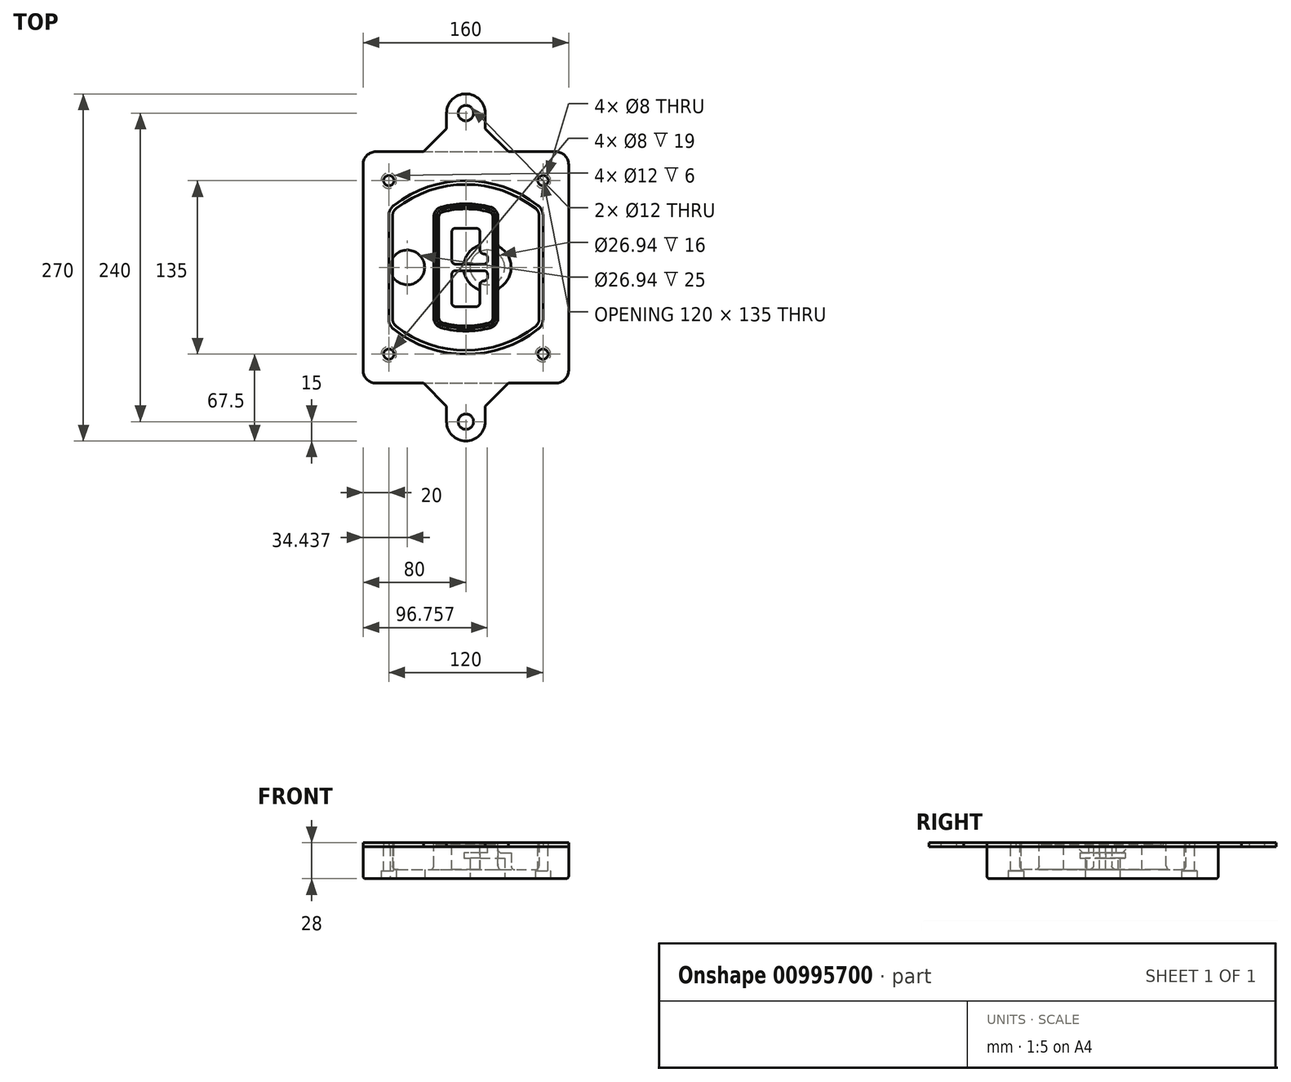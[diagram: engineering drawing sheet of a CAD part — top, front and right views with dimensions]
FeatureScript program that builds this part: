
annotation { "Feature Type Name" : "Feature", "Feature Type Description" : "" }
export const myFeature = defineFeature(function(context is Context, id is Id, definition is map)
    precondition{}
    {
        {
            var Q0;
            Q0=qCreatedBy(makeId("Top.planeOp"),FACE);
            var sketch = newSketch(context, id + "F0", { "sketchPlane" : qUnion([Q0])});
            skPoint(sketch, "E0.rect.middle", {"position": v(0, 0) * mm});
            skLineSegment(sketch, "E1.bottom", {"start": v(-70, -90) * mm, "end": v(70, -90) * mm});
            skLineSegment(sketch, "E1.top", {"start": v(-70, 90) * mm, "end": v(70, 90) * mm});
            skLineSegment(sketch, "E1.left", {"start": v(-80, -80) * mm, "end": v(-80, 80) * mm});
            skLineSegment(sketch, "E1.right", {"start": v(80, -80) * mm, "end": v(80, 80) * mm});
            skLineSegment(sketch, "E2", {"start": v(-80, 90) * mm, "end": v(80, -90) * mm, "construction": true});
            skLineSegment(sketch, "E3", {"start": v(80, 90) * mm, "end": v(-80, -90) * mm, "construction": true});
            skCircle(sketch, "E4", {"center": v(-60, 67.5) * mm, "radius": 4 * mm});
            skCircle(sketch, "E5", {"center": v(60, 67.5) * mm, "radius": 4 * mm});
            skCircle(sketch, "E6", {"center": v(60, -67.5) * mm, "radius": 4 * mm});
            skCircle(sketch, "E7", {"center": v(-60, -67.5) * mm, "radius": 4 * mm});
            skLineSegment(sketch, "E8", {"start": v(-60, 67.5) * mm, "end": v(60, 67.5) * mm, "construction": true});
            skLineSegment(sketch, "E9", {"start": v(60, 67.5) * mm, "end": v(60, -67.5) * mm, "construction": true});
            skLineSegment(sketch, "E10", {"start": v(60, -67.5) * mm, "end": v(-60, -67.5) * mm, "construction": true});
            skLineSegment(sketch, "E11", {"start": v(-60, -67.5) * mm, "end": v(-60, 67.5) * mm, "construction": true});
            skLineSegment(sketch, "E12", {"start": v(-60, 40.3) * mm, "end": v(-60, -40.3) * mm});
            skLineSegment(sketch, "E13", {"start": v(60, 40.3) * mm, "end": v(60, -40.3) * mm});
            skArc(sketch, "E14", {"start": v(56.15, 48.18) * mm, "mid": v(0, 67.5) * mm, "end": v(-56.15, 48.18) * mm});
            skArc(sketch, "E15", {"start": v(-56.15, -48.18) * mm, "mid": v(0, -67.5) * mm, "end": v(56.15, -48.18) * mm});
            skLineSegment(sketch, "E16", {"start": v(-60, 0) * mm, "end": v(60, 0) * mm, "construction": true});
            skPoint(sketch, "E17.visualSharp", {"position": v(-60, -45) * mm});
            skArc(sketch, "E17.filletArc", {"start": v(-60, -40.3) * mm, "mid": v(-58.99, -44.68) * mm, "end": v(-56.15, -48.18) * mm});
            skPoint(sketch, "E18.visualSharp", {"position": v(-60, 45) * mm});
            skArc(sketch, "E18.filletArc", {"start": v(-56.15, 48.18) * mm, "mid": v(-58.99, 44.68) * mm, "end": v(-60, 40.3) * mm});
            skPoint(sketch, "E19.visualSharp", {"position": v(60, 45) * mm});
            skArc(sketch, "E19.filletArc", {"start": v(60, 40.3) * mm, "mid": v(58.99, 44.68) * mm, "end": v(56.15, 48.18) * mm});
            skPoint(sketch, "E20.visualSharp", {"position": v(60, -45) * mm});
            skArc(sketch, "E20.filletArc", {"start": v(56.15, -48.18) * mm, "mid": v(58.99, -44.68) * mm, "end": v(60, -40.3) * mm});
            skPoint(sketch, "E21.visualSharp", {"position": v(-80, 90) * mm});
            skArc(sketch, "E21.filletArc", {"start": v(-70, 90) * mm, "mid": v(-77.07, 87.07) * mm, "end": v(-80, 80) * mm});
            skPoint(sketch, "E22.visualSharp", {"position": v(80, 90) * mm});
            skArc(sketch, "E22.filletArc", {"start": v(80, 80) * mm, "mid": v(77.07, 87.07) * mm, "end": v(70, 90) * mm});
            skPoint(sketch, "E23.visualSharp", {"position": v(80, -90) * mm});
            skArc(sketch, "E23.filletArc", {"start": v(70, -90) * mm, "mid": v(77.07, -87.07) * mm, "end": v(80, -80) * mm});
            skPoint(sketch, "E24.visualSharp", {"position": v(-80, -90) * mm});
            skArc(sketch, "E24.filletArc", {"start": v(-80, -80) * mm, "mid": v(-77.07, -87.07) * mm, "end": v(-70, -90) * mm});
            skArc(sketch, "E25.0", {"start": v(57, 40.3) * mm, "mid": v(56.3, 43.36) * mm, "end": v(54.3, 45.81) * mm});
            skLineSegment(sketch, "E25.1", {"start": v(57, 40.3) * mm, "end": v(57, -40.3) * mm});
            skArc(sketch, "E25.2", {"start": v(54.3, -45.81) * mm, "mid": v(56.3, -43.36) * mm, "end": v(57, -40.3) * mm});
            skArc(sketch, "E25.3", {"start": v(-54.3, -45.81) * mm, "mid": v(0, -64.5) * mm, "end": v(54.3, -45.81) * mm});
            skArc(sketch, "E25.4", {"start": v(-57, -40.3) * mm, "mid": v(-56.3, -43.36) * mm, "end": v(-54.3, -45.81) * mm});
            skArc(sketch, "E25.5", {"start": v(54.3, 45.81) * mm, "mid": v(0, 64.5) * mm, "end": v(-54.3, 45.81) * mm});
            skLineSegment(sketch, "E25.6", {"start": v(-57, 40.3) * mm, "end": v(-57, -40.3) * mm});
            skArc(sketch, "E25.7", {"start": v(-54.3, 45.81) * mm, "mid": v(-56.3, 43.36) * mm, "end": v(-57, 40.3) * mm});
            skArc(sketch, "E26.0", {"start": v(-58.62, 51.33) * mm, "mid": v(-62.58, 46.43) * mm, "end": v(-64, 40.3) * mm});
            skArc(sketch, "E26.1", {"start": v(58.62, 51.33) * mm, "mid": v(0, 71.5) * mm, "end": v(-58.62, 51.33) * mm});
            skArc(sketch, "E26.2", {"start": v(64, 40.3) * mm, "mid": v(62.58, 46.43) * mm, "end": v(58.62, 51.33) * mm});
            skLineSegment(sketch, "E26.3", {"start": v(64, 40.3) * mm, "end": v(64, -40.3) * mm});
            skArc(sketch, "E26.4", {"start": v(58.62, -51.33) * mm, "mid": v(62.58, -46.43) * mm, "end": v(64, -40.3) * mm});
            skLineSegment(sketch, "E26.5", {"start": v(-64, 40.3) * mm, "end": v(-64, -40.3) * mm});
            skArc(sketch, "E26.6", {"start": v(-58.62, -51.33) * mm, "mid": v(0, -71.5) * mm, "end": v(58.62, -51.33) * mm});
            skArc(sketch, "E26.7", {"start": v(-64, -40.3) * mm, "mid": v(-62.58, -46.43) * mm, "end": v(-58.62, -51.33) * mm});
            skSolve(sketch);
        }
        {
            var Q0;
            Q0=makeQuery(id+"F0.imprint","IMPRINT",FACE,{"disambiguationData":[TD([[makeQuery(id+"F0.imprint","IMPRINT",EDGE,{"derivedFrom":sQuery(id+"F0.wireOp",EDGE,"E1.bottom")}),1.0]])]});
            var Q1;
            Q1=makeQuery(id+"F0.imprint","IMPRINT",FACE,{"disambiguationData":[TD([[makeQuery(id+"F0.imprint","IMPRINT",EDGE,{"derivedFrom":sQuery(id+"F0.wireOp",EDGE,"E12")}),1.0]])]});
            var Q2;
            Q2=makeQuery(id+"F0.imprint","IMPRINT",FACE,{"disambiguationData":[TD([[makeQuery(id+"F0.imprint","IMPRINT",EDGE,{"derivedFrom":sQuery(id+"F0.wireOp",EDGE,"E25.0")}),1.0]])]});
            var Q3;
            Q3=makeQuery(id+"F0.imprint","IMPRINT",FACE,{"disambiguationData":[TD([[makeQuery(id+"F0.imprint","IMPRINT",EDGE,{"derivedFrom":sQuery(id+"F0.wireOp",EDGE,"E12")}),-1.0]])]});
            extrude(context, id + "F1", {"entities" : qUnion([Q0, Q1, Q2, Q3]), "oppositeDirection" : true, "depth" : 25 * mm});
        }
        {
            var Q0;
            Q0=makeQuery(id+"F0.imprint","IMPRINT",FACE,{"disambiguationData":[TD([[makeQuery(id+"F0.imprint","IMPRINT",EDGE,{"derivedFrom":sQuery(id+"F0.wireOp",EDGE,"E12")}),1.0]])]});
            extrude(context, id + "F2", {"entities" : qUnion([Q0]), "operationType" : NewBodyOperationType.ADD, "depth" : 3 * mm});
        }
        {
            var Q0;
            Q0=makeQuery(id+"F0.imprint","IMPRINT",FACE,{"disambiguationData":[TD([[makeQuery(id+"F0.imprint","IMPRINT",EDGE,{"derivedFrom":sQuery(id+"F0.wireOp",EDGE,"E25.0")}),1.0]])]});
            extrude(context, id + "F3", {"entities" : qUnion([Q0]), "operationType" : NewBodyOperationType.REMOVE, "oppositeDirection" : true, "depth" : 18 * mm});
        }
        {
            var Q0;
            Q0=makeQuery(id+"F2.opExtrude","CAP_FACE",FACE,{"disambiguationData":[OSD([sQuery(id+"F0.wireOp",EDGE,"E12"),sQuery(id+"F0.wireOp",EDGE,"E13"),sQuery(id+"F0.wireOp",EDGE,"E14"),sQuery(id+"F0.wireOp",EDGE,"E15"),sQuery(id+"F0.wireOp",EDGE,"E17.filletArc"),sQuery(id+"F0.wireOp",EDGE,"E18.filletArc"),sQuery(id+"F0.wireOp",EDGE,"E19.filletArc"),sQuery(id+"F0.wireOp",EDGE,"E20.filletArc"),sQuery(id+"F0.wireOp",EDGE,"E25.0"),sQuery(id+"F0.wireOp",EDGE,"E25.1"),sQuery(id+"F0.wireOp",EDGE,"E25.2"),sQuery(id+"F0.wireOp",EDGE,"E25.3"),sQuery(id+"F0.wireOp",EDGE,"E25.4"),sQuery(id+"F0.wireOp",EDGE,"E25.5"),sQuery(id+"F0.wireOp",EDGE,"E25.6"),sQuery(id+"F0.wireOp",EDGE,"E25.7")])],"isStart":false});
            var sketch = newSketch(context, id + "F4", { "sketchPlane" : qUnion([Q0])});
            skArc(sketch, "E27.0", {"start": v(-19.08, -46.97) * mm, "mid": v(0, -49.5) * mm, "end": v(19.08, -46.97) * mm});
            skArc(sketch, "E28.0", {"start": v(19.08, 46.97) * mm, "mid": v(0, 49.5) * mm, "end": v(-19.08, 46.97) * mm});
            skLineSegment(sketch, "E29", {"start": v(-25, 39.25) * mm, "end": v(-25, -39.25) * mm});
            skLineSegment(sketch, "E30", {"start": v(25, 39.25) * mm, "end": v(25, -39.25) * mm});
            skLineSegment(sketch, "E31", {"start": v(-25, 45.1) * mm, "end": v(25, 45.1) * mm, "construction": true});
            skLineSegment(sketch, "E32", {"start": v(-25, -45.1) * mm, "end": v(25, -45.1) * mm, "construction": true});
            skPoint(sketch, "E33.visualSharp", {"position": v(-25, 45.1) * mm});
            skArc(sketch, "E33.filletArc", {"start": v(-19.08, 46.97) * mm, "mid": v(-23.35, 44.11) * mm, "end": v(-25, 39.25) * mm});
            skPoint(sketch, "E34.visualSharp", {"position": v(25, 45.1) * mm});
            skArc(sketch, "E34.filletArc", {"start": v(25, 39.25) * mm, "mid": v(23.35, 44.11) * mm, "end": v(19.08, 46.97) * mm});
            skPoint(sketch, "E35.visualSharp", {"position": v(25, -45.1) * mm});
            skArc(sketch, "E35.filletArc", {"start": v(19.08, -46.97) * mm, "mid": v(23.35, -44.11) * mm, "end": v(25, -39.25) * mm});
            skPoint(sketch, "E36.visualSharp", {"position": v(-25, -45.1) * mm});
            skArc(sketch, "E36.filletArc", {"start": v(-25, -39.25) * mm, "mid": v(-23.35, -44.11) * mm, "end": v(-19.08, -46.97) * mm});
            skArc(sketch, "E37.0", {"start": v(54.3, 45.81) * mm, "mid": v(0, 64.5) * mm, "end": v(-54.3, 45.81) * mm});
            skArc(sketch, "E37.1", {"start": v(-54.3, 45.81) * mm, "mid": v(-56.3, 43.36) * mm, "end": v(-57, 40.3) * mm});
            skLineSegment(sketch, "E37.2", {"start": v(-57, 40.3) * mm, "end": v(-57, -40.3) * mm});
            skArc(sketch, "E37.3", {"start": v(-57, -40.3) * mm, "mid": v(-56.3, -43.36) * mm, "end": v(-54.3, -45.81) * mm});
            skArc(sketch, "E37.4", {"start": v(-54.3, -45.81) * mm, "mid": v(0, -64.5) * mm, "end": v(54.3, -45.81) * mm});
            skArc(sketch, "E37.5", {"start": v(54.3, -45.81) * mm, "mid": v(56.3, -43.36) * mm, "end": v(57, -40.3) * mm});
            skLineSegment(sketch, "E37.6", {"start": v(57, 40.3) * mm, "end": v(57, -40.3) * mm});
            skArc(sketch, "E37.7", {"start": v(57, 40.3) * mm, "mid": v(56.3, 43.36) * mm, "end": v(54.3, 45.81) * mm});
            skLineSegment(sketch, "E38.0", {"start": v(23, 39.25) * mm, "end": v(23, -39.25) * mm});
            skArc(sketch, "E38.1", {"start": v(18.56, -45.04) * mm, "mid": v(21.76, -42.9) * mm, "end": v(23, -39.25) * mm});
            skArc(sketch, "E38.2", {"start": v(-18.56, -45.04) * mm, "mid": v(0, -47.5) * mm, "end": v(18.56, -45.04) * mm});
            skArc(sketch, "E38.3", {"start": v(-23, -39.25) * mm, "mid": v(-21.76, -42.9) * mm, "end": v(-18.56, -45.04) * mm});
            skLineSegment(sketch, "E38.4", {"start": v(-23, 39.25) * mm, "end": v(-23, -39.25) * mm});
            skArc(sketch, "E38.5", {"start": v(23, 39.25) * mm, "mid": v(21.76, 42.9) * mm, "end": v(18.56, 45.04) * mm});
            skArc(sketch, "E38.6", {"start": v(-18.56, 45.04) * mm, "mid": v(-21.76, 42.9) * mm, "end": v(-23, 39.25) * mm});
            skArc(sketch, "E38.7", {"start": v(18.56, 45.04) * mm, "mid": v(0, 47.5) * mm, "end": v(-18.56, 45.04) * mm});
            skArc(sketch, "E39.0", {"start": v(21, 39.25) * mm, "mid": v(20.18, 41.68) * mm, "end": v(18.04, 43.1) * mm});
            skLineSegment(sketch, "E39.1", {"start": v(21, 39.25) * mm, "end": v(21, -39.25) * mm});
            skArc(sketch, "E39.2", {"start": v(18.04, -43.1) * mm, "mid": v(20.18, -41.68) * mm, "end": v(21, -39.25) * mm});
            skArc(sketch, "E39.3", {"start": v(-18.04, -43.1) * mm, "mid": v(0, -45.5) * mm, "end": v(18.04, -43.1) * mm});
            skArc(sketch, "E39.4", {"start": v(-21, -39.25) * mm, "mid": v(-20.18, -41.68) * mm, "end": v(-18.04, -43.1) * mm});
            skArc(sketch, "E39.5", {"start": v(18.04, 43.1) * mm, "mid": v(0, 45.5) * mm, "end": v(-18.04, 43.1) * mm});
            skLineSegment(sketch, "E39.6", {"start": v(-21, 39.25) * mm, "end": v(-21, -39.25) * mm});
            skArc(sketch, "E39.7", {"start": v(-18.04, 43.1) * mm, "mid": v(-20.18, 41.68) * mm, "end": v(-21, 39.25) * mm});
            skLineSegment(sketch, "E40", {"start": v(-25, 0) * mm, "end": v(25, 0) * mm, "construction": true});
            skLineSegment(sketch, "E41", {"start": v(-11, 5.5) * mm, "end": v(-11, 27.5) * mm});
            skLineSegment(sketch, "E42", {"start": v(-8, 30.5) * mm, "end": v(8, 30.5) * mm});
            skLineSegment(sketch, "E43", {"start": v(11, 27.5) * mm, "end": v(11, 13.5) * mm});
            skLineSegment(sketch, "E44", {"start": v(14, 10.5) * mm, "end": v(14, 10.5) * mm});
            skLineSegment(sketch, "E45", {"start": v(17, 7.5) * mm, "end": v(17, 5.5) * mm});
            skLineSegment(sketch, "E46", {"start": v(14, 2.5) * mm, "end": v(-8, 2.5) * mm});
            skPoint(sketch, "E47.visualSharp", {"position": v(-11, 30.5) * mm});
            skArc(sketch, "E47.filletArc", {"start": v(-8, 30.5) * mm, "mid": v(-10.12, 29.62) * mm, "end": v(-11, 27.5) * mm});
            skPoint(sketch, "E48.visualSharp", {"position": v(11, 30.5) * mm});
            skArc(sketch, "E48.filletArc", {"start": v(11, 27.5) * mm, "mid": v(10.12, 29.62) * mm, "end": v(8, 30.5) * mm});
            skPoint(sketch, "E49.visualSharp", {"position": v(11, 10.5) * mm});
            skArc(sketch, "E49.filletArc", {"start": v(11, 13.5) * mm, "mid": v(11.88, 11.38) * mm, "end": v(14, 10.5) * mm});
            skPoint(sketch, "E50.visualSharp", {"position": v(17, 10.5) * mm});
            skArc(sketch, "E50.filletArc", {"start": v(17, 7.5) * mm, "mid": v(16.12, 9.62) * mm, "end": v(14, 10.5) * mm});
            skPoint(sketch, "E51.visualSharp", {"position": v(17, 2.5) * mm});
            skArc(sketch, "E51.filletArc", {"start": v(14, 2.5) * mm, "mid": v(16.12, 3.38) * mm, "end": v(17, 5.5) * mm});
            skPoint(sketch, "E52.visualSharp", {"position": v(-11, 2.5) * mm});
            skArc(sketch, "E52.filletArc", {"start": v(-11, 5.5) * mm, "mid": v(-10.12, 3.38) * mm, "end": v(-8, 2.5) * mm});
            skLineSegment(sketch, "E53.0.MirrorCS", {"start": v(14, -2.5) * mm, "end": v(-8, -2.5) * mm});
            skArc(sketch, "E54.0.MirrorCS", {"start": v(-11, -5.5) * mm, "mid": v(-10.12, -3.38) * mm, "end": v(-8, -2.5) * mm});
            skLineSegment(sketch, "E55.0.MirrorCS", {"start": v(-11, -5.5) * mm, "end": v(-11, -27.5) * mm});
            skArc(sketch, "E56.0.MirrorCS", {"start": v(-8, -30.5) * mm, "mid": v(-10.12, -29.62) * mm, "end": v(-11, -27.5) * mm});
            skLineSegment(sketch, "E57.0.MirrorCS", {"start": v(-8, -30.5) * mm, "end": v(8, -30.5) * mm});
            skArc(sketch, "E58.0.MirrorCS", {"start": v(11, -27.5) * mm, "mid": v(10.12, -29.62) * mm, "end": v(8, -30.5) * mm});
            skLineSegment(sketch, "E59.0.MirrorCS", {"start": v(11, -27.5) * mm, "end": v(11, -13.5) * mm});
            skArc(sketch, "E60.0.MirrorCS", {"start": v(11, -13.5) * mm, "mid": v(11.88, -11.38) * mm, "end": v(14, -10.5) * mm});
            skArc(sketch, "E61.0.MirrorCS", {"start": v(17, -7.5) * mm, "mid": v(16.12, -9.62) * mm, "end": v(14, -10.5) * mm});
            skLineSegment(sketch, "E62.0.MirrorCS", {"start": v(17, -7.5) * mm, "end": v(17, -5.5) * mm});
            skArc(sketch, "E63.0.MirrorCS", {"start": v(14, -2.5) * mm, "mid": v(16.12, -3.38) * mm, "end": v(17, -5.5) * mm});
            skSolve(sketch);
        }
        {
            var Q0;
            Q0=makeQuery(id+"F4.imprint","IMPRINT",FACE,{"disambiguationData":[TD([[makeQuery(id+"F4.imprint","IMPRINT",EDGE,{"derivedFrom":sQuery(id+"F4.wireOp",EDGE,"E27.0")}),1.0]])]});
            var Q1;
            Q1=makeQuery(id+"F4.imprint","IMPRINT",FACE,{"disambiguationData":[TD([[makeQuery(id+"F4.imprint","IMPRINT",EDGE,{"derivedFrom":sQuery(id+"F4.wireOp",EDGE,"E38.0")}),-1.0]])]});
            var Q2;
            Q2=makeQuery(id+"F4.imprint","IMPRINT",FACE,{"disambiguationData":[TD([[makeQuery(id+"F4.imprint","IMPRINT",EDGE,{"derivedFrom":sQuery(id+"F4.wireOp",EDGE,"E39.0")}),1.0]])]});
            extrude(context, id + "F5", {"entities" : qUnion([Q0, Q1, Q2]), "operationType" : NewBodyOperationType.ADD, "endBound" : BoundingType.UP_TO_NEXT, "oppositeDirection" : true, "depth" : 25 * mm});
        }
        {
            var Q0;
            Q0=makeQuery(id+"F4.imprint","IMPRINT",FACE,{"disambiguationData":[TD([[makeQuery(id+"F4.imprint","IMPRINT",EDGE,{"derivedFrom":sQuery(id+"F4.wireOp",EDGE,"E38.0")}),-1.0]])]});
            extrude(context, id + "F6", {"entities" : qUnion([Q0]), "operationType" : NewBodyOperationType.REMOVE, "oppositeDirection" : true, "depth" : 2 * mm});
        }
        {
            var Q0;
            Q0=makeQuery(id+"F1.opExtrude","CAP_FACE",FACE,{"disambiguationData":[OSD([sQuery(id+"F0.wireOp",EDGE,"E1.bottom"),sQuery(id+"F0.wireOp",EDGE,"E1.top"),sQuery(id+"F0.wireOp",EDGE,"E1.left"),sQuery(id+"F0.wireOp",EDGE,"E1.right"),sQuery(id+"F0.wireOp",EDGE,"E4"),sQuery(id+"F0.wireOp",EDGE,"E5"),sQuery(id+"F0.wireOp",EDGE,"E6"),sQuery(id+"F0.wireOp",EDGE,"E7"),sQuery(id+"F0.wireOp",EDGE,"E21.filletArc"),sQuery(id+"F0.wireOp",EDGE,"E22.filletArc"),sQuery(id+"F0.wireOp",EDGE,"E23.filletArc"),sQuery(id+"F0.wireOp",EDGE,"E24.filletArc")])],"isStart":false});
            var sketch = newSketch(context, id + "F7", { "sketchPlane" : qUnion([Q0])});
            skCircle(sketch, "E64", {"center": v(16.76, 0) * mm, "radius": 13.47 * mm});
            skCircle(sketch, "E65", {"center": v(-45.56, 0) * mm, "radius": 13.47 * mm});
            skLineSegment(sketch, "E66", {"start": v(80, 0) * mm, "end": v(-80, 0) * mm});
            skCircle(sketch, "E67", {"center": v(16.76, 0) * mm, "radius": 18.47 * mm});
            skCircle(sketch, "E68", {"center": v(60, -67.5) * mm, "radius": 6 * mm});
            skCircle(sketch, "E69", {"center": v(-60, -67.5) * mm, "radius": 6 * mm});
            skCircle(sketch, "E70", {"center": v(-60, 67.5) * mm, "radius": 6 * mm});
            skCircle(sketch, "E71", {"center": v(60, 67.5) * mm, "radius": 6 * mm});
            skSolve(sketch);
        }
        {
            var Q0;
            {var subQ1=sQuery(id+"F7.wireOp",EDGE,"E66");var subQ4=sQuery(id+"F7.wireOp",EDGE,"E64");var subQ6=makeQuery(id+"F7.imprint","INTERSECT",VERTEX,{"disambiguationData":[OD(0.0)],"derivedFrom":[subQ4,subQ1]});Q0=makeQuery(id+"F7.imprint","IMPRINT",FACE,{"disambiguationData":[TD([[makeQuery(id+"F7.imprint","IMPRINT",EDGE,{"disambiguationData":[TD([[subQ6,-1.0]])],"derivedFrom":subQ4}),-1.0]])]});}
            var Q1;
            {var subQ0=sQuery(id+"F7.wireOp",EDGE,"E66");var subQ1=sQuery(id+"F7.wireOp",EDGE,"E64");var subQ3=makeQuery(id+"F7.imprint","INTERSECT",VERTEX,{"disambiguationData":[OD(0.0)],"derivedFrom":[subQ1,subQ0]});Q1=makeQuery(id+"F7.imprint","IMPRINT",FACE,{"disambiguationData":[TD([[makeQuery(id+"F7.imprint","IMPRINT",EDGE,{"disambiguationData":[TD([[subQ3,-1.0]])],"derivedFrom":subQ1}),1.0]])]});}
            var Q2;
            {var subQ0=sQuery(id+"F7.wireOp",EDGE,"E66");var subQ1=sQuery(id+"F7.wireOp",EDGE,"E64");var subQ3=makeQuery(id+"F7.imprint","INTERSECT",VERTEX,{"disambiguationData":[OD(0.0)],"derivedFrom":[subQ1,subQ0]});Q2=makeQuery(id+"F7.imprint","IMPRINT",FACE,{"disambiguationData":[TD([[makeQuery(id+"F7.imprint","IMPRINT",EDGE,{"disambiguationData":[TD([[subQ3,1.0]])],"derivedFrom":subQ1}),1.0]])]});}
            var Q3;
            {var subQ1=sQuery(id+"F7.wireOp",EDGE,"E66");var subQ4=sQuery(id+"F7.wireOp",EDGE,"E64");var subQ6=makeQuery(id+"F7.imprint","INTERSECT",VERTEX,{"disambiguationData":[OD(0.0)],"derivedFrom":[subQ4,subQ1]});Q3=makeQuery(id+"F7.imprint","IMPRINT",FACE,{"disambiguationData":[TD([[makeQuery(id+"F7.imprint","IMPRINT",EDGE,{"disambiguationData":[TD([[subQ6,1.0]])],"derivedFrom":subQ4}),-1.0]])]});}
            extrude(context, id + "F8", {"entities" : qUnion([Q0, Q1, Q2, Q3]), "operationType" : NewBodyOperationType.ADD, "oppositeDirection" : true, "depth" : 20 * mm});
        }
        {
            var Q0;
            {var subQ0=sQuery(id+"F7.wireOp",EDGE,"E66");var subQ1=sQuery(id+"F7.wireOp",EDGE,"E64");var subQ3=makeQuery(id+"F7.imprint","INTERSECT",VERTEX,{"disambiguationData":[OD(0.0)],"derivedFrom":[subQ1,subQ0]});Q0=makeQuery(id+"F7.imprint","IMPRINT",FACE,{"disambiguationData":[TD([[makeQuery(id+"F7.imprint","IMPRINT",EDGE,{"disambiguationData":[TD([[subQ3,-1.0]])],"derivedFrom":subQ1}),1.0]])]});}
            var Q1;
            {var subQ0=sQuery(id+"F7.wireOp",EDGE,"E66");var subQ1=sQuery(id+"F7.wireOp",EDGE,"E64");var subQ3=makeQuery(id+"F7.imprint","INTERSECT",VERTEX,{"disambiguationData":[OD(0.0)],"derivedFrom":[subQ1,subQ0]});Q1=makeQuery(id+"F7.imprint","IMPRINT",FACE,{"disambiguationData":[TD([[makeQuery(id+"F7.imprint","IMPRINT",EDGE,{"disambiguationData":[TD([[subQ3,1.0]])],"derivedFrom":subQ1}),1.0]])]});}
            extrude(context, id + "F9", {"entities" : qUnion([Q0, Q1]), "operationType" : NewBodyOperationType.REMOVE, "oppositeDirection" : true, "depth" : 16 * mm});
        }
        {
            var Q0;
            {var subQ0=sQuery(id+"F7.wireOp",EDGE,"E66");var subQ1=sQuery(id+"F7.wireOp",EDGE,"E65");var subQ3=makeQuery(id+"F7.imprint","INTERSECT",VERTEX,{"disambiguationData":[OD(0.0)],"derivedFrom":[subQ1,subQ0]});Q0=makeQuery(id+"F7.imprint","IMPRINT",FACE,{"disambiguationData":[TD([[makeQuery(id+"F7.imprint","IMPRINT",EDGE,{"disambiguationData":[TD([[subQ3,-1.0]])],"derivedFrom":subQ1}),1.0]])]});}
            var Q1;
            {var subQ0=sQuery(id+"F7.wireOp",EDGE,"E66");var subQ1=sQuery(id+"F7.wireOp",EDGE,"E65");var subQ3=makeQuery(id+"F7.imprint","INTERSECT",VERTEX,{"disambiguationData":[OD(0.0)],"derivedFrom":[subQ1,subQ0]});Q1=makeQuery(id+"F7.imprint","IMPRINT",FACE,{"disambiguationData":[TD([[makeQuery(id+"F7.imprint","IMPRINT",EDGE,{"disambiguationData":[TD([[subQ3,1.0]])],"derivedFrom":subQ1}),1.0]])]});}
            extrude(context, id + "F10", {"entities" : qUnion([Q0, Q1]), "operationType" : NewBodyOperationType.REMOVE, "oppositeDirection" : true, "depth" : 25 * mm});
        }
        {
            var Q0;
            Q0=makeQuery(id+"F7.imprint","IMPRINT",FACE,{"disambiguationData":[TD([[makeQuery(id+"F7.imprint","IMPRINT",EDGE,{"derivedFrom":sQuery(id+"F7.wireOp",EDGE,"E68")}),1.0]])]});
            var Q1;
            Q1=makeQuery(id+"F7.imprint","IMPRINT",FACE,{"disambiguationData":[TD([[makeQuery(id+"F7.imprint","IMPRINT",EDGE,{"derivedFrom":makeQuery(id+"F1.opExtrude","CAP_EDGE",EDGE,{"disambiguationData":[OSD([sQuery(id+"F0.wireOp",EDGE,"E5")])],"isStart":false})}),-1.0]])]});
            var Q2;
            Q2=makeQuery(id+"F7.imprint","IMPRINT",FACE,{"disambiguationData":[TD([[makeQuery(id+"F7.imprint","IMPRINT",EDGE,{"derivedFrom":sQuery(id+"F7.wireOp",EDGE,"E69")}),1.0]])]});
            var Q3;
            Q3=makeQuery(id+"F7.imprint","IMPRINT",FACE,{"disambiguationData":[TD([[makeQuery(id+"F7.imprint","IMPRINT",EDGE,{"derivedFrom":makeQuery(id+"F1.opExtrude","CAP_EDGE",EDGE,{"disambiguationData":[OSD([sQuery(id+"F0.wireOp",EDGE,"E4")])],"isStart":false})}),-1.0]])]});
            var Q4;
            Q4=makeQuery(id+"F7.imprint","IMPRINT",FACE,{"disambiguationData":[TD([[makeQuery(id+"F7.imprint","IMPRINT",EDGE,{"derivedFrom":sQuery(id+"F7.wireOp",EDGE,"E70")}),1.0]])]});
            var Q5;
            Q5=makeQuery(id+"F7.imprint","IMPRINT",FACE,{"disambiguationData":[TD([[makeQuery(id+"F7.imprint","IMPRINT",EDGE,{"derivedFrom":makeQuery(id+"F1.opExtrude","CAP_EDGE",EDGE,{"disambiguationData":[OSD([sQuery(id+"F0.wireOp",EDGE,"E7")])],"isStart":false})}),-1.0]])]});
            var Q6;
            Q6=makeQuery(id+"F7.imprint","IMPRINT",FACE,{"disambiguationData":[TD([[makeQuery(id+"F7.imprint","IMPRINT",EDGE,{"derivedFrom":sQuery(id+"F7.wireOp",EDGE,"E71")}),1.0]])]});
            var Q7;
            Q7=makeQuery(id+"F7.imprint","IMPRINT",FACE,{"disambiguationData":[TD([[makeQuery(id+"F7.imprint","IMPRINT",EDGE,{"derivedFrom":makeQuery(id+"F1.opExtrude","CAP_EDGE",EDGE,{"disambiguationData":[OSD([sQuery(id+"F0.wireOp",EDGE,"E6")])],"isStart":false})}),-1.0]])]});
            extrude(context, id + "F11", {"entities" : qUnion([Q0, Q1, Q2, Q3, Q4, Q5, Q6, Q7]), "operationType" : NewBodyOperationType.REMOVE, "oppositeDirection" : true, "depth" : 6 * mm});
        }
        {
            var Q0;
            Q0=makeQuery(id+"F9.boolean.opBoolean","COPY",FACE,{"derivedFrom":makeQuery(id+"F9.opExtrude","CAP_FACE",FACE,{"disambiguationData":[OSD([sQuery(id+"F7.wireOp",EDGE,"E64")])],"isStart":false})});
            var sketch = newSketch(context, id + "F12", { "sketchPlane" : qUnion([Q0])});
            skArc(sketch, "E72.0", {"start": v(11, 17.55) * mm, "mid": v(2.57, 11.82) * mm, "end": v(-1.54, 2.5) * mm});
            skArc(sketch, "E72.1", {"start": v(-1.54, -2.5) * mm, "mid": v(2.57, -11.82) * mm, "end": v(11, -17.55) * mm});
            skLineSegment(sketch, "E73", {"start": v(-1.54, -2.5) * mm, "end": v(14, -2.5) * mm});
            skLineSegment(sketch, "E74.0", {"start": v(14, 2.5) * mm, "end": v(-1.54, 2.5) * mm});
            skArc(sketch, "E74.1", {"start": v(14, 2.5) * mm, "mid": v(16.12, 3.38) * mm, "end": v(17, 5.5) * mm});
            skLineSegment(sketch, "E74.2", {"start": v(17, 7.5) * mm, "end": v(17, 5.5) * mm});
            skArc(sketch, "E74.3", {"start": v(17, 7.5) * mm, "mid": v(16.12, 9.62) * mm, "end": v(14, 10.5) * mm});
            skArc(sketch, "E74.4", {"start": v(11, 13.5) * mm, "mid": v(11.88, 11.38) * mm, "end": v(14, 10.5) * mm});
            skLineSegment(sketch, "E74.5", {"start": v(11, 17.55) * mm, "end": v(11, 13.5) * mm});
            skLineSegment(sketch, "E74.7", {"start": v(14, -2.5) * mm, "end": v(-1.54, -2.5) * mm});
            skArc(sketch, "E74.8", {"start": v(14, -2.5) * mm, "mid": v(16.12, -3.38) * mm, "end": v(17, -5.5) * mm});
            skLineSegment(sketch, "E74.9", {"start": v(17, -7.5) * mm, "end": v(17, -5.5) * mm});
            skArc(sketch, "E74.10", {"start": v(17, -7.5) * mm, "mid": v(16.12, -9.62) * mm, "end": v(14, -10.5) * mm});
            skArc(sketch, "E74.11", {"start": v(11, -13.5) * mm, "mid": v(11.88, -11.38) * mm, "end": v(14, -10.5) * mm});
            skLineSegment(sketch, "E74.12", {"start": v(11, -17.55) * mm, "end": v(11, -13.5) * mm});
            skPoint(sketch, "E75.orphan", {"position": v(11, -27.5) * mm});
            skPoint(sketch, "E76.orphan", {"position": v(-8, -2.5) * mm});
            skPoint(sketch, "E77.orphan", {"position": v(-8, 2.5) * mm});
            skPoint(sketch, "E78.orphan", {"position": v(11, 27.5) * mm});
            skSolve(sketch);
        }
        {
            var Q0;
            {var subQ7=sQuery(id+"F12.wireOp",EDGE,"E72.0");var subQ14=sQuery(id+"F12.wireOp",EDGE,"E72.1");var subQ16=sQuery(id+"F12.wireOp",EDGE,"E74.1");var subQ18=sQuery(id+"F12.wireOp",EDGE,"E74.8");Q0=qUnion([makeQuery(id+"F12.imprint","IMPRINT",FACE,{"disambiguationData":[TD([[makeQuery(id+"F12.imprint","IMPRINT",EDGE,{"derivedFrom":subQ7}),1.0]])]}),makeQuery(id+"F12.imprint","IMPRINT",FACE,{"disambiguationData":[TD([[makeQuery(id+"F12.imprint","IMPRINT",EDGE,{"derivedFrom":subQ14}),1.0]])]}),makeQuery(id+"F12.imprint","IMPRINT",FACE,{"disambiguationData":[TD([[makeQuery(id+"F12.imprint","IMPRINT",EDGE,{"derivedFrom":subQ16}),1.0]])]}),makeQuery(id+"F12.imprint","IMPRINT",FACE,{"disambiguationData":[TD([[makeQuery(id+"F12.imprint","IMPRINT",EDGE,{"derivedFrom":subQ18}),-1.0]])]})]);}
            var Q1;
            Q1=makeQuery(id+"F5.boolean.opBoolean","SPLIT",FACE,{"disambiguationData":[TD([makeQuery(id+"F5.opExtrude","SWEPT_FACE",FACE,{"disambiguationData":[OSD([sQuery(id+"F4.wireOp",EDGE,"E41")])]})])],"derivedFrom":makeQuery(id+"F3.boolean.opBoolean","COPY",FACE,{"derivedFrom":makeQuery(id+"F3.opExtrude","CAP_FACE",FACE,{"disambiguationData":[OSD([sQuery(id+"F0.wireOp",EDGE,"E25.0"),sQuery(id+"F0.wireOp",EDGE,"E25.1"),sQuery(id+"F0.wireOp",EDGE,"E25.2"),sQuery(id+"F0.wireOp",EDGE,"E25.3"),sQuery(id+"F0.wireOp",EDGE,"E25.4"),sQuery(id+"F0.wireOp",EDGE,"E25.5"),sQuery(id+"F0.wireOp",EDGE,"E25.6"),sQuery(id+"F0.wireOp",EDGE,"E25.7")])],"isStart":false})})});
            extrude(context, id + "F13", {"entities" : qUnion([Q0]), "operationType" : NewBodyOperationType.REMOVE, "endBound" : BoundingType.UP_TO_SURFACE, "endBoundEntityFace" : qUnion([Q1]), "depth" : 25 * mm});
        }
        {
            var Q0;
            Q0=makeQuery(id+"F3.boolean.opBoolean","COPY",EDGE,{"derivedFrom":makeQuery(id+"F3.opExtrude","CAP_EDGE",EDGE,{"disambiguationData":[OSD([sQuery(id+"F0.wireOp",EDGE,"E25.6")])],"isStart":false})});
            var Q1;
            Q1=makeQuery(id+"F8.boolean.opBoolean","INTERSECT",EDGE,{"derivedFrom":[makeQuery(id+"F5.opExtrude","SWEPT_FACE",FACE,{"disambiguationData":[OSD([sQuery(id+"F4.wireOp",EDGE,"E30")])]}),makeQuery(id+"F8.opExtrude","CAP_FACE",FACE,{"disambiguationData":[OSD([sQuery(id+"F7.wireOp",EDGE,"E67")])],"isStart":false})]});
            var Q2;
            Q2=makeQuery(id+"F8.boolean.opBoolean","INTERSECT",EDGE,{"disambiguationData":[OD(1.0)],"derivedFrom":[makeQuery(id+"F5.opExtrude","SWEPT_FACE",FACE,{"disambiguationData":[OSD([sQuery(id+"F4.wireOp",EDGE,"E30")])]}),makeQuery(id+"F8.opExtrude","SWEPT_FACE",FACE,{"disambiguationData":[OSD([sQuery(id+"F7.wireOp",EDGE,"E67")])]})]});
            var Q3;
            {var subQ0=sQuery(id+"F4.wireOp",EDGE,"E30");Q3=makeQuery(id+"F8.boolean.opBoolean","SPLIT",EDGE,{"disambiguationData":[TD([makeQuery(id+"F5.opExtrude","SWEPT_FACE",FACE,{"disambiguationData":[OSD([sQuery(id+"F4.wireOp",EDGE,"E35.filletArc")])]})])],"derivedFrom":makeQuery(id+"F5.opExtrude","CAP_EDGE",EDGE,{"disambiguationData":[OSD([subQ0])],"isStart":false})});}
            var Q4;
            {var subQ0=sQuery(id+"F0.wireOp",EDGE,"E25.7");var subQ1=sQuery(id+"F0.wireOp",EDGE,"E25.1");var subQ2=sQuery(id+"F0.wireOp",EDGE,"E25.6");var subQ3=sQuery(id+"F0.wireOp",EDGE,"E25.5");var subQ4=sQuery(id+"F0.wireOp",EDGE,"E25.4");var subQ5=sQuery(id+"F0.wireOp",EDGE,"E25.0");var subQ6=sQuery(id+"F0.wireOp",EDGE,"E25.2");var subQ7=sQuery(id+"F0.wireOp",EDGE,"E25.3");Q4=makeQuery(id+"F8.boolean.opBoolean","INTERSECT",EDGE,{"derivedFrom":[makeQuery(id+"F5.boolean.opBoolean","SPLIT",FACE,{"disambiguationData":[TD([makeQuery(id+"F2.opExtrude","SWEPT_FACE",FACE,{"disambiguationData":[OSD([subQ5])]})])],"derivedFrom":makeQuery(id+"F3.boolean.opBoolean","COPY",FACE,{"derivedFrom":makeQuery(id+"F3.opExtrude","CAP_FACE",FACE,{"disambiguationData":[OSD([subQ5,subQ1,subQ6,subQ7,subQ4,subQ3,subQ2,subQ0])],"isStart":false})})}),makeQuery(id+"F8.opExtrude","SWEPT_FACE",FACE,{"disambiguationData":[OSD([sQuery(id+"F7.wireOp",EDGE,"E67")])]})]});}
            var Q5;
            Q5=makeQuery(id+"F8.boolean.opBoolean","INTERSECT",EDGE,{"disambiguationData":[OD(0.0)],"derivedFrom":[makeQuery(id+"F5.opExtrude","SWEPT_FACE",FACE,{"disambiguationData":[OSD([sQuery(id+"F4.wireOp",EDGE,"E30")])]}),makeQuery(id+"F8.opExtrude","SWEPT_FACE",FACE,{"disambiguationData":[OSD([sQuery(id+"F7.wireOp",EDGE,"E67")])]})]});
            fillet(context, id + "F14", {"entities" : qUnion([Q0, Q1, Q2, Q3, Q4, Q5]), "radius" : 3 * mm, "tangentPropagation" : true, "allowEdgeOverflow" : false});
        }
        {
            var Q0;
            Q0=makeQuery(id+"F1.opExtrude","CAP_EDGE",EDGE,{"disambiguationData":[OSD([sQuery(id+"F0.wireOp",EDGE,"E1.bottom")])],"isStart":false});
            fillet(context, id + "F15", {"entities" : qUnion([Q0]), "radius" : 2 * mm, "tangentPropagation" : true, "allowEdgeOverflow" : false});
        }
        {
            var Q0;
            {var subQ0=sQuery(id+"F0.wireOp",EDGE,"E21.filletArc");var subQ1=sQuery(id+"F0.wireOp",EDGE,"E7");var subQ2=sQuery(id+"F0.wireOp",EDGE,"E6");var subQ3=sQuery(id+"F0.wireOp",EDGE,"E5");var subQ4=sQuery(id+"F0.wireOp",EDGE,"E4");var subQ5=sQuery(id+"F0.wireOp",EDGE,"E22.filletArc");var subQ6=sQuery(id+"F0.wireOp",EDGE,"E1.bottom");var subQ7=sQuery(id+"F0.wireOp",EDGE,"E1.right");var subQ8=sQuery(id+"F0.wireOp",EDGE,"E1.top");var subQ9=sQuery(id+"F0.wireOp",EDGE,"E1.left");var subQ10=sQuery(id+"F0.wireOp",EDGE,"E23.filletArc");var subQ11=sQuery(id+"F0.wireOp",EDGE,"E24.filletArc");Q0=makeQuery(id+"F2.boolean.opBoolean","SPLIT",FACE,{"disambiguationData":[TD([makeQuery(id+"F1.opExtrude","SWEPT_FACE",FACE,{"disambiguationData":[OSD([subQ6])]})])],"derivedFrom":makeQuery(id+"F1.opExtrude","CAP_FACE",FACE,{"disambiguationData":[OSD([subQ6,subQ8,subQ9,subQ7,subQ4,subQ3,subQ2,subQ1,subQ0,subQ5,subQ10,subQ11])],"isStart":true})});}
            var sketch = newSketch(context, id + "F16", { "sketchPlane" : qUnion([Q0])});
            skCircle(sketch, "E79", {"center": v(0, 120) * mm, "radius": 6 * mm});
            skLineSegment(sketch, "E80", {"start": v(-33, 90) * mm, "end": v(-15, 108) * mm});
            skLineSegment(sketch, "E81", {"start": v(-15, 108) * mm, "end": v(-15, 120) * mm});
            skLineSegment(sketch, "E82", {"start": v(33, 90) * mm, "end": v(15, 108) * mm});
            skLineSegment(sketch, "E83", {"start": v(15, 108) * mm, "end": v(15, 120) * mm});
            skArc(sketch, "E84", {"start": v(15, 120) * mm, "mid": v(0, 135) * mm, "end": v(-15, 120) * mm});
            skCircle(sketch, "E85.0", {"center": v(-60, 67.5) * mm, "radius": 4 * mm});
            skCircle(sketch, "E86.0", {"center": v(60, 67.5) * mm, "radius": 4 * mm});
            skLineSegment(sketch, "E87.0.0", {"start": v(70, 90) * mm, "end": v(-70, 90) * mm});
            skArc(sketch, "E87.0.1", {"start": v(-70, 90) * mm, "mid": v(-77.07, 87.07) * mm, "end": v(-80, 80) * mm});
            skLineSegment(sketch, "E87.0.2", {"start": v(-80, 80) * mm, "end": v(-80, -80) * mm});
            skArc(sketch, "E87.0.3", {"start": v(-80, -80) * mm, "mid": v(-77.07, -87.07) * mm, "end": v(-70, -90) * mm});
            skLineSegment(sketch, "E87.0.4", {"start": v(-70, -90) * mm, "end": v(70, -90) * mm});
            skArc(sketch, "E87.0.5", {"start": v(70, -90) * mm, "mid": v(77.07, -87.07) * mm, "end": v(80, -80) * mm});
            skLineSegment(sketch, "E87.0.6", {"start": v(80, -80) * mm, "end": v(80, 80) * mm});
            skArc(sketch, "E87.0.7", {"start": v(80, 80) * mm, "mid": v(77.07, 87.07) * mm, "end": v(70, 90) * mm});
            skCircle(sketch, "E88.0", {"center": v(-60, -67.5) * mm, "radius": 4 * mm});
            skCircle(sketch, "E89.0", {"center": v(60, -67.5) * mm, "radius": 4 * mm});
            skLineSegment(sketch, "E90", {"start": v(-80, 0) * mm, "end": v(80, 0) * mm, "construction": true});
            skPoint(sketch, "E90.startSnap0", {"position": v(-80, 0) * mm});
            skLineSegment(sketch, "E91.MirrorCS", {"start": v(-33, -90) * mm, "end": v(-15, -108) * mm});
            skLineSegment(sketch, "E92.MirrorCS", {"start": v(-15, -108) * mm, "end": v(-15, -120) * mm});
            skArc(sketch, "E93.MirrorCS", {"start": v(15, -120) * mm, "mid": v(0, -135) * mm, "end": v(-15, -120) * mm});
            skLineSegment(sketch, "E94.MirrorCS", {"start": v(15, -108) * mm, "end": v(15, -120) * mm});
            skLineSegment(sketch, "E95.MirrorCS", {"start": v(33, -90) * mm, "end": v(15, -108) * mm});
            skCircle(sketch, "E96.MirrorC", {"center": v(0, -120) * mm, "radius": 6 * mm});
            skLineSegment(sketch, "E97.0", {"start": v(-60, 40.3) * mm, "end": v(-60, -40.3) * mm});
            skArc(sketch, "E98.0", {"start": v(-56.15, 48.18) * mm, "mid": v(-58.99, 44.68) * mm, "end": v(-60, 40.3) * mm});
            skArc(sketch, "E99.0", {"start": v(56.15, 48.18) * mm, "mid": v(0, 67.5) * mm, "end": v(-56.15, 48.18) * mm});
            skLineSegment(sketch, "E100.0", {"start": v(60, 40.3) * mm, "end": v(60, -40.3) * mm});
            skLineSegment(sketch, "E101.0.0", {"start": v(60, -40.3) * mm, "end": v(60, 40.3) * mm});
            skArc(sketch, "E101.0.1", {"start": v(60, 40.3) * mm, "mid": v(58.99, 44.68) * mm, "end": v(56.15, 48.18) * mm});
            skArc(sketch, "E101.0.5", {"start": v(-60, -40.3) * mm, "mid": v(-58.99, -44.68) * mm, "end": v(-56.15, -48.18) * mm});
            skArc(sketch, "E101.0.6", {"start": v(-56.15, -48.18) * mm, "mid": v(0, -67.5) * mm, "end": v(56.15, -48.18) * mm});
            skArc(sketch, "E101.0.7", {"start": v(56.15, -48.18) * mm, "mid": v(58.99, -44.68) * mm, "end": v(60, -40.3) * mm});
            skSolve(sketch);
        }
        {
            var Q0;
            Q0 = qSketchRegion(id + "F16", true);
            var Q1;
            Q1=makeQuery(id+"F2.opExtrude","CAP_FACE",FACE,{"disambiguationData":[OSD([sQuery(id+"F0.wireOp",EDGE,"E12"),sQuery(id+"F0.wireOp",EDGE,"E13"),sQuery(id+"F0.wireOp",EDGE,"E14"),sQuery(id+"F0.wireOp",EDGE,"E15"),sQuery(id+"F0.wireOp",EDGE,"E17.filletArc"),sQuery(id+"F0.wireOp",EDGE,"E18.filletArc"),sQuery(id+"F0.wireOp",EDGE,"E19.filletArc"),sQuery(id+"F0.wireOp",EDGE,"E20.filletArc"),sQuery(id+"F0.wireOp",EDGE,"E25.0"),sQuery(id+"F0.wireOp",EDGE,"E25.1"),sQuery(id+"F0.wireOp",EDGE,"E25.2"),sQuery(id+"F0.wireOp",EDGE,"E25.3"),sQuery(id+"F0.wireOp",EDGE,"E25.4"),sQuery(id+"F0.wireOp",EDGE,"E25.5"),sQuery(id+"F0.wireOp",EDGE,"E25.6"),sQuery(id+"F0.wireOp",EDGE,"E25.7")])],"isStart":false});
            extrude(context, id + "F17", {"entities" : qUnion([Q0]), "endBound" : BoundingType.UP_TO_SURFACE, "depth" : 25 * mm, "endBoundEntityFace" : qUnion([Q1]), "offsetDistance" : 25 * mm});
        }
    });
